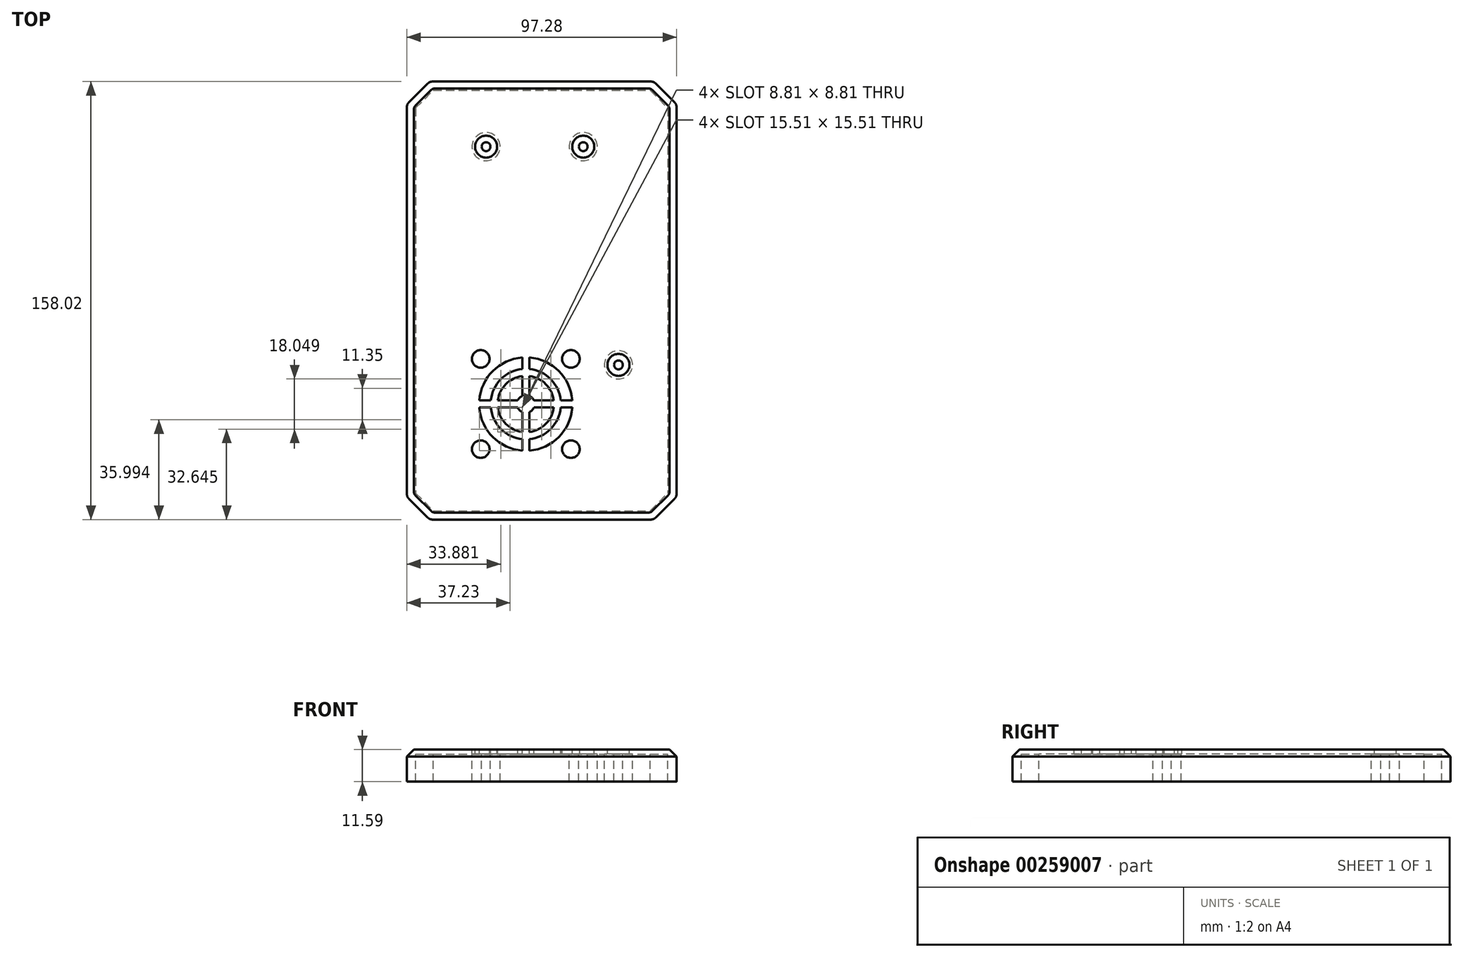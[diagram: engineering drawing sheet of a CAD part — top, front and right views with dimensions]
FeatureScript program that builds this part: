
annotation { "Feature Type Name" : "Feature", "Feature Type Description" : "" }
export const myFeature = defineFeature(function(context is Context, id is Id, definition is map)
    precondition{}
    {
        {
            var Q0;
            Q0=qCreatedBy(makeId("Top.planeOp"),FACE);
            var sketch = newSketch(context, id + "F0", { "sketchPlane" : qUnion([Q0])});
            skLineSegment(sketch, "E0.bottom", {"start": v(-39.11, 75.84) * mm, "end": v(39.11, 75.84) * mm});
            skLineSegment(sketch, "E0.top", {"start": v(-39.11, -75.84) * mm, "end": v(39.11, -75.84) * mm});
            skLineSegment(sketch, "E0.left", {"start": v(-45.46, 69.49) * mm, "end": v(-45.46, -69.49) * mm});
            skLineSegment(sketch, "E0.right", {"start": v(45.46, 69.49) * mm, "end": v(45.46, -69.49) * mm});
            skLineSegment(sketch, "E1", {"start": v(-45.46, 69.49) * mm, "end": v(-39.11, 75.84) * mm});
            skLineSegment(sketch, "E2", {"start": v(39.11, 75.84) * mm, "end": v(45.46, 69.49) * mm});
            skLineSegment(sketch, "E3", {"start": v(-45.46, -69.49) * mm, "end": v(-39.11, -75.84) * mm});
            skLineSegment(sketch, "E4", {"start": v(39.11, -75.84) * mm, "end": v(45.46, -69.49) * mm});
            skPoint(sketch, "E5.orphan", {"position": v(-45.46, 75.84) * mm});
            skPoint(sketch, "E6.orphan", {"position": v(45.46, 75.84) * mm});
            skPoint(sketch, "E7.orphan", {"position": v(45.46, -75.84) * mm});
            skPoint(sketch, "E8.orphan", {"position": v(-45.46, -75.84) * mm});
            skLineSegment(sketch, "E9.0", {"start": v(-48.64, 70.8) * mm, "end": v(-40.43, 79.01) * mm});
            skLineSegment(sketch, "E9.1", {"start": v(-40.43, 79.01) * mm, "end": v(40.43, 79.01) * mm});
            skLineSegment(sketch, "E9.2", {"start": v(-48.64, 70.8) * mm, "end": v(-48.64, -70.8) * mm});
            skLineSegment(sketch, "E9.3", {"start": v(40.43, 79.01) * mm, "end": v(48.64, 70.8) * mm});
            skLineSegment(sketch, "E9.4", {"start": v(-48.64, -70.8) * mm, "end": v(-40.43, -79.01) * mm});
            skLineSegment(sketch, "E9.5", {"start": v(-40.43, -79.01) * mm, "end": v(40.43, -79.01) * mm});
            skLineSegment(sketch, "E9.6", {"start": v(40.43, -79.01) * mm, "end": v(48.64, -70.8) * mm});
            skLineSegment(sketch, "E9.7", {"start": v(48.64, 70.8) * mm, "end": v(48.64, -70.8) * mm});
            skSolve(sketch);
        }
        {
            var Q0;
            Q0=qCreatedBy(makeId("Top.planeOp"),FACE);
            var sketch = newSketch(context, id + "F1", { "sketchPlane" : qUnion([Q0])});
            skCircle(sketch, "E10", {"center": v(-20.06, 55.52) * mm, "radius": 5.08 * mm});
            skCircle(sketch, "E11", {"center": v(14.98, 55.52) * mm, "radius": 5.08 * mm});
            skCircle(sketch, "E12", {"center": v(27.68, -23.22) * mm, "radius": 5.08 * mm});
            skCircle(sketch, "E13", {"center": v(-20.06, 55.52) * mm, "radius": 1.59 * mm});
            skCircle(sketch, "E14", {"center": v(14.98, 55.52) * mm, "radius": 1.59 * mm});
            skCircle(sketch, "E15", {"center": v(27.68, -23.22) * mm, "radius": 1.59 * mm});
            skSolve(sketch);
        }
        {
            var Q0;
            Q0=makeQuery(id+"FWIGaCaiah2UGG0_0.opExtrude","CAP_FACE",FACE,{"disambiguationData":[OSD([sQuery(id+"F0.wireOp",EDGE,"E9.0"),sQuery(id+"F0.wireOp",EDGE,"E9.1"),sQuery(id+"F0.wireOp",EDGE,"E9.2"),sQuery(id+"F0.wireOp",EDGE,"E9.3"),sQuery(id+"F0.wireOp",EDGE,"E9.4"),sQuery(id+"F0.wireOp",EDGE,"E9.5"),sQuery(id+"F0.wireOp",EDGE,"E9.6"),sQuery(id+"F0.wireOp",EDGE,"E9.7")])],"isStart":true});
            var sketch = newSketch(context, id + "F2", { "sketchPlane" : qUnion([Q0])});
            skLineSegment(sketch, "E16.bottom", {"start": v(-39.29, 12.34) * mm, "end": v(10.71, 12.34) * mm});
            skLineSegment(sketch, "E16.top", {"start": v(-39.29, -72.66) * mm, "end": v(10.71, -72.66) * mm});
            skLineSegment(sketch, "E16.left", {"start": v(-42.29, 9.34) * mm, "end": v(-42.29, -69.66) * mm});
            skLineSegment(sketch, "E16.right", {"start": v(13.71, 9.34) * mm, "end": v(13.71, -69.66) * mm});
            skCircle(sketch, "E17", {"center": v(-38.79, -69.16) * mm, "radius": 3.1 * mm});
            skCircle(sketch, "E18", {"center": v(10.21, -69.16) * mm, "radius": 3.1 * mm});
            skCircle(sketch, "E19", {"center": v(10.21, -11.16) * mm, "radius": 3.1 * mm});
            skCircle(sketch, "E20", {"center": v(-38.79, -11.16) * mm, "radius": 3.1 * mm});
            skCircle(sketch, "E21", {"center": v(-38.79, -11.16) * mm, "radius": 1.38 * mm});
            skCircle(sketch, "E22", {"center": v(10.21, -11.16) * mm, "radius": 1.38 * mm});
            skCircle(sketch, "E23", {"center": v(10.21, -69.16) * mm, "radius": 1.38 * mm});
            skCircle(sketch, "E24", {"center": v(-38.79, -69.16) * mm, "radius": 1.38 * mm});
            skPoint(sketch, "E25.visualSharp", {"position": v(-42.29, 12.34) * mm});
            skArc(sketch, "E25.filletArc", {"start": v(-39.29, 12.34) * mm, "mid": v(-41.4, 11.46) * mm, "end": v(-42.29, 9.34) * mm});
            skPoint(sketch, "E26.visualSharp", {"position": v(13.71, 12.34) * mm});
            skArc(sketch, "E26.filletArc", {"start": v(13.71, 9.34) * mm, "mid": v(12.83, 11.46) * mm, "end": v(10.71, 12.34) * mm});
            skPoint(sketch, "E27.visualSharp", {"position": v(-42.29, -72.66) * mm});
            skArc(sketch, "E27.filletArc", {"start": v(-42.29, -69.66) * mm, "mid": v(-41.4, -71.78) * mm, "end": v(-39.29, -72.66) * mm});
            skPoint(sketch, "E28.visualSharp", {"position": v(13.71, -72.66) * mm});
            skArc(sketch, "E28.filletArc", {"start": v(10.71, -72.66) * mm, "mid": v(12.83, -71.78) * mm, "end": v(13.71, -69.66) * mm});
            skSolve(sketch);
        }
        {
            var Q0;
            Q0=makeQuery(id+"F0.imprint","IMPRINT",FACE,{"disambiguationData":[TD([[makeQuery(id+"F0.imprint","IMPRINT",EDGE,{"derivedFrom":sQuery(id+"F0.wireOp",EDGE,"E0.bottom")}),-1.0]])]});
            var Q1;
            Q1=makeQuery(id+"F0.imprint","IMPRINT",FACE,{"disambiguationData":[TD([[makeQuery(id+"F0.imprint","IMPRINT",EDGE,{"derivedFrom":sQuery(id+"F0.wireOp",EDGE,"E0.bottom")}),1.0]])]});
            extrude(context, id + "F3", {"entities" : qUnion([Q0, Q1]), "depth" : 1.59 * mm});
        }
        {
            var Q0;
            Q0=makeQuery(id+"F1.imprint","IMPRINT",FACE,{"disambiguationData":[TD([[makeQuery(id+"F1.imprint","IMPRINT",EDGE,{"derivedFrom":sQuery(id+"F1.wireOp",EDGE,"E12")}),1.0]])]});
            var Q1;
            Q1=makeQuery(id+"F1.imprint","IMPRINT",FACE,{"disambiguationData":[TD([[makeQuery(id+"F1.imprint","IMPRINT",EDGE,{"derivedFrom":sQuery(id+"F1.wireOp",EDGE,"E11")}),1.0]])]});
            var Q2;
            Q2=makeQuery(id+"F1.imprint","IMPRINT",FACE,{"disambiguationData":[TD([[makeQuery(id+"F1.imprint","IMPRINT",EDGE,{"derivedFrom":sQuery(id+"F1.wireOp",EDGE,"E10")}),1.0]])]});
            extrude(context, id + "F4", {"entities" : qUnion([Q0, Q1, Q2]), "operationType" : NewBodyOperationType.ADD, "oppositeDirection" : true, "depth" : 10 * mm});
        }
        {
            var Q0;
            Q0 = qSketchRegion(id + "F2", true);
            var Q1;
            Q1 = qSketchRegion(id + "F0", true);
            extrude(context, id + "F5", {"entities" : qUnion([Q0, Q1]), "operationType" : NewBodyOperationType.ADD, "oppositeDirection" : true, "depth" : 10 * mm});
        }
        {
            var Q0;
            Q0=makeQuery(id+"F3.opExtrude","CAP_FACE",FACE,{"disambiguationData":[OSD([sQuery(id+"F0.wireOp",EDGE,"E9.0"),sQuery(id+"F0.wireOp",EDGE,"E9.1"),sQuery(id+"F0.wireOp",EDGE,"E9.2"),sQuery(id+"F0.wireOp",EDGE,"E9.3"),sQuery(id+"F0.wireOp",EDGE,"E9.4"),sQuery(id+"F0.wireOp",EDGE,"E9.5"),sQuery(id+"F0.wireOp",EDGE,"E9.6"),sQuery(id+"F0.wireOp",EDGE,"E9.7")])],"isStart":false});
            var sketch = newSketch(context, id + "F6", { "sketchPlane" : qUnion([Q0])});
            skCircle(sketch, "E29", {"center": v(-20.06, 55.52) * mm, "radius": 3.97 * mm});
            skCircle(sketch, "E30", {"center": v(14.98, 55.52) * mm, "radius": 3.97 * mm});
            skCircle(sketch, "E31", {"center": v(27.68, -23.22) * mm, "radius": 3.97 * mm});
            skSolve(sketch);
        }
        {
            var Q0;
            Q0 = qSketchRegion(id + "F6", true);
            extrude(context, id + "F7", {"entities" : qUnion([Q0]), "operationType" : NewBodyOperationType.REMOVE, "oppositeDirection" : true, "depth" : 1.59 * mm});
        }
        {
            var Q0;
            Q0=makeQuery(id+"F3.opExtrude","CAP_FACE",FACE,{"disambiguationData":[OSD([sQuery(id+"F0.wireOp",EDGE,"E9.0"),sQuery(id+"F0.wireOp",EDGE,"E9.1"),sQuery(id+"F0.wireOp",EDGE,"E9.2"),sQuery(id+"F0.wireOp",EDGE,"E9.3"),sQuery(id+"F0.wireOp",EDGE,"E9.4"),sQuery(id+"F0.wireOp",EDGE,"E9.5"),sQuery(id+"F0.wireOp",EDGE,"E9.6"),sQuery(id+"F0.wireOp",EDGE,"E9.7")])],"isStart":false});
            var sketch = newSketch(context, id + "F8", { "sketchPlane" : qUnion([Q0])});
            skCircle(sketch, "E32", {"center": v(-22, -21.07) * mm, "radius": 3.18 * mm});
            skCircle(sketch, "E33", {"center": v(10.54, -21.07) * mm, "radius": 3.18 * mm});
            skCircle(sketch, "E34", {"center": v(10.54, -53.61) * mm, "radius": 3.18 * mm});
            skCircle(sketch, "E35", {"center": v(-22, -53.61) * mm, "radius": 3.18 * mm});
            skArc(sketch, "E36", {"start": v(-22.51, -38.61) * mm, "mid": v(-17.63, -49.24) * mm, "end": v(-7, -54.12) * mm});
            skArc(sketch, "E37", {"start": v(-7, -34.43) * mm, "mid": v(-7.98, -35.1) * mm, "end": v(-8.64, -36.07) * mm});
            skLineSegment(sketch, "E38", {"start": v(-7, -34.43) * mm, "end": v(-7, -27.26) * mm});
            skLineSegment(sketch, "E39", {"start": v(-4.46, -34.43) * mm, "end": v(-4.46, -27.26) * mm});
            skLineSegment(sketch, "E40", {"start": v(-2.82, -36.07) * mm, "end": v(4.35, -36.07) * mm});
            skLineSegment(sketch, "E41", {"start": v(-2.82, -38.61) * mm, "end": v(4.35, -38.61) * mm});
            skLineSegment(sketch, "E42", {"start": v(-7, -40.25) * mm, "end": v(-7, -47.42) * mm});
            skLineSegment(sketch, "E43", {"start": v(-4.46, -40.25) * mm, "end": v(-4.46, -47.42) * mm});
            skLineSegment(sketch, "E44", {"start": v(-8.64, -36.07) * mm, "end": v(-15.81, -36.07) * mm});
            skLineSegment(sketch, "E45", {"start": v(-8.64, -38.61) * mm, "end": v(-15.81, -38.61) * mm});
            skArc(sketch, "E46", {"start": v(-15.81, -38.61) * mm, "mid": v(-12.92, -44.52) * mm, "end": v(-7, -47.42) * mm});
            skArc(sketch, "E47", {"start": v(-18.37, -38.61) * mm, "mid": v(-14.71, -46.32) * mm, "end": v(-7, -49.98) * mm});
            skLineSegment(sketch, "E48.trimOffspring", {"start": v(-18.37, -36.07) * mm, "end": v(-22.51, -36.07) * mm});
            skLineSegment(sketch, "E49.trimOffspring", {"start": v(-18.37, -38.61) * mm, "end": v(-22.51, -38.61) * mm});
            skArc(sketch, "E50.trimOffspring", {"start": v(4.35, -36.07) * mm, "mid": v(1.45, -30.16) * mm, "end": v(-4.46, -27.26) * mm});
            skArc(sketch, "E51.trimOffspring", {"start": v(6.9, -36.07) * mm, "mid": v(3.25, -28.36) * mm, "end": v(-4.46, -24.7) * mm});
            skLineSegment(sketch, "E52.trimOffspring", {"start": v(6.9, -36.07) * mm, "end": v(11.05, -36.07) * mm});
            skLineSegment(sketch, "E53.trimOffspring", {"start": v(6.9, -38.61) * mm, "end": v(11.05, -38.61) * mm});
            skLineSegment(sketch, "E54.trimOffspring", {"start": v(-4.46, -24.7) * mm, "end": v(-4.46, -20.56) * mm});
            skLineSegment(sketch, "E55.trimOffspring", {"start": v(-7, -24.7) * mm, "end": v(-7, -20.56) * mm});
            skArc(sketch, "E56.trimOffspring", {"start": v(-7, -24.7) * mm, "mid": v(-14.71, -28.36) * mm, "end": v(-18.37, -36.07) * mm});
            skArc(sketch, "E57.trimOffspring", {"start": v(-7, -27.26) * mm, "mid": v(-12.92, -30.16) * mm, "end": v(-15.81, -36.07) * mm});
            skArc(sketch, "E58.trimOffspring", {"start": v(-8.64, -38.61) * mm, "mid": v(-7.98, -39.59) * mm, "end": v(-7, -40.25) * mm});
            skArc(sketch, "E59.trimOffspring", {"start": v(-2.82, -36.07) * mm, "mid": v(-3.49, -35.1) * mm, "end": v(-4.46, -34.43) * mm});
            skArc(sketch, "E60.trimOffspring", {"start": v(-4.46, -40.25) * mm, "mid": v(-3.49, -39.59) * mm, "end": v(-2.82, -38.61) * mm});
            skLineSegment(sketch, "E61.trimOffspring", {"start": v(-7, -49.98) * mm, "end": v(-7, -54.12) * mm});
            skLineSegment(sketch, "E62.trimOffspring", {"start": v(-4.46, -49.98) * mm, "end": v(-4.46, -54.12) * mm});
            skArc(sketch, "E63.trimOffspring", {"start": v(-7, -20.56) * mm, "mid": v(-17.63, -25.44) * mm, "end": v(-22.51, -36.07) * mm});
            skArc(sketch, "E64.trimOffspring", {"start": v(11.05, -36.07) * mm, "mid": v(6.16, -25.44) * mm, "end": v(-4.46, -20.56) * mm});
            skArc(sketch, "E65.trimOffspring", {"start": v(-4.46, -54.12) * mm, "mid": v(6.16, -49.24) * mm, "end": v(11.05, -38.61) * mm});
            skArc(sketch, "E66.trimOffspring", {"start": v(-4.46, -49.98) * mm, "mid": v(3.25, -46.32) * mm, "end": v(6.9, -38.61) * mm});
            skArc(sketch, "E67.trimOffspring", {"start": v(-4.46, -47.42) * mm, "mid": v(1.45, -44.52) * mm, "end": v(4.35, -38.61) * mm});
            skSolve(sketch);
        }
        {
            var Q0;
            Q0 = qSketchRegion(id + "F8", true);
            extrude(context, id + "F9", {"entities" : qUnion([Q0]), "operationType" : NewBodyOperationType.REMOVE, "endBound" : BoundingType.THROUGH_ALL, "oppositeDirection" : true, "depth" : 25.4 * mm});
        }
        {
            var Q0;
            Q0=makeQuery(id+"F3.opExtrude","CAP_EDGE",EDGE,{"disambiguationData":[OSD([sQuery(id+"F0.wireOp",EDGE,"E9.1")])],"isStart":false});
            var Q1;
            Q1=makeQuery(id+"F3.opExtrude","CAP_EDGE",EDGE,{"disambiguationData":[OSD([sQuery(id+"F0.wireOp",EDGE,"E9.0")])],"isStart":false});
            var Q2;
            Q2=makeQuery(id+"F3.opExtrude","CAP_EDGE",EDGE,{"disambiguationData":[OSD([sQuery(id+"F0.wireOp",EDGE,"E9.2")])],"isStart":false});
            var Q3;
            Q3=makeQuery(id+"F3.opExtrude","CAP_EDGE",EDGE,{"disambiguationData":[OSD([sQuery(id+"F0.wireOp",EDGE,"E9.3")])],"isStart":false});
            var Q4;
            Q4=makeQuery(id+"F3.opExtrude","CAP_EDGE",EDGE,{"disambiguationData":[OSD([sQuery(id+"F0.wireOp",EDGE,"E9.7")])],"isStart":false});
            var Q5;
            Q5=makeQuery(id+"F3.opExtrude","CAP_EDGE",EDGE,{"disambiguationData":[OSD([sQuery(id+"F0.wireOp",EDGE,"E9.4")])],"isStart":false});
            var Q6;
            Q6=makeQuery(id+"F3.opExtrude","CAP_EDGE",EDGE,{"disambiguationData":[OSD([sQuery(id+"F0.wireOp",EDGE,"E9.5")])],"isStart":false});
            var Q7;
            Q7=makeQuery(id+"F3.opExtrude","CAP_EDGE",EDGE,{"disambiguationData":[OSD([sQuery(id+"F0.wireOp",EDGE,"E9.6")])],"isStart":false});
            chamfer(context, id + "F10", {"entities" : qUnion([Q0, Q1, Q2, Q3, Q4, Q5, Q6, Q7]), "width" : 2.54 * mm, "tangentPropagation" : true});
        }
        {
            var Q0;
            {var subQ0=sQuery(id+"F0.wireOp",EDGE,"E9.7");var subQ1=sQuery(id+"F0.wireOp",EDGE,"E9.3");Q0=makeQuery(id+"F5.boolean.opBoolean","MERGE",EDGE,{"derivedFrom":[makeQuery(id+"F3.opExtrude","SWEPT_EDGE",EDGE,{"disambiguationData":[OSD([subQ1,subQ0])]}),makeQuery(id+"F5.opExtrude","SWEPT_EDGE",EDGE,{"disambiguationData":[OSD([subQ1,subQ0])]})]});}
            var Q1;
            Q1=makeQuery(id+"F10.opChamfer","BLEND_EDGE",EDGE,{"blendedFrom":[makeQuery(id+"F3.opExtrude","CAP_EDGE",EDGE,{"disambiguationData":[OSD([sQuery(id+"F0.wireOp",EDGE,"E9.3")])],"isStart":false}),makeQuery(id+"F3.opExtrude","CAP_EDGE",EDGE,{"disambiguationData":[OSD([sQuery(id+"F0.wireOp",EDGE,"E9.7")])],"isStart":false})],"blendedInto":[]});
            var Q2;
            {var subQ0=sQuery(id+"F0.wireOp",EDGE,"E9.3");var subQ1=sQuery(id+"F0.wireOp",EDGE,"E9.1");Q2=makeQuery(id+"F5.boolean.opBoolean","MERGE",EDGE,{"derivedFrom":[makeQuery(id+"F3.opExtrude","SWEPT_EDGE",EDGE,{"disambiguationData":[OSD([subQ1,subQ0])]}),makeQuery(id+"F5.opExtrude","SWEPT_EDGE",EDGE,{"disambiguationData":[OSD([subQ1,subQ0])]})]});}
            var Q3;
            Q3=makeQuery(id+"F10.opChamfer","BLEND_EDGE",EDGE,{"blendedFrom":[makeQuery(id+"F3.opExtrude","CAP_EDGE",EDGE,{"disambiguationData":[OSD([sQuery(id+"F0.wireOp",EDGE,"E9.1")])],"isStart":false}),makeQuery(id+"F3.opExtrude","CAP_EDGE",EDGE,{"disambiguationData":[OSD([sQuery(id+"F0.wireOp",EDGE,"E9.3")])],"isStart":false})],"blendedInto":[]});
            var Q4;
            {var subQ0=sQuery(id+"F0.wireOp",EDGE,"E9.1");var subQ1=sQuery(id+"F0.wireOp",EDGE,"E9.0");Q4=makeQuery(id+"F5.boolean.opBoolean","MERGE",EDGE,{"derivedFrom":[makeQuery(id+"F3.opExtrude","SWEPT_EDGE",EDGE,{"disambiguationData":[OSD([subQ1,subQ0])]}),makeQuery(id+"F5.opExtrude","SWEPT_EDGE",EDGE,{"disambiguationData":[OSD([subQ1,subQ0])]})]});}
            var Q5;
            Q5=makeQuery(id+"F10.opChamfer","BLEND_EDGE",EDGE,{"blendedFrom":[makeQuery(id+"F3.opExtrude","CAP_EDGE",EDGE,{"disambiguationData":[OSD([sQuery(id+"F0.wireOp",EDGE,"E9.0")])],"isStart":false}),makeQuery(id+"F3.opExtrude","CAP_EDGE",EDGE,{"disambiguationData":[OSD([sQuery(id+"F0.wireOp",EDGE,"E9.1")])],"isStart":false})],"blendedInto":[]});
            var Q6;
            Q6=makeQuery(id+"F10.opChamfer","BLEND_EDGE",EDGE,{"blendedFrom":[makeQuery(id+"F3.opExtrude","CAP_EDGE",EDGE,{"disambiguationData":[OSD([sQuery(id+"F0.wireOp",EDGE,"E9.0")])],"isStart":false}),makeQuery(id+"F3.opExtrude","CAP_EDGE",EDGE,{"disambiguationData":[OSD([sQuery(id+"F0.wireOp",EDGE,"E9.2")])],"isStart":false})],"blendedInto":[]});
            var Q7;
            {var subQ0=sQuery(id+"F0.wireOp",EDGE,"E9.2");var subQ1=sQuery(id+"F0.wireOp",EDGE,"E9.0");Q7=makeQuery(id+"F5.boolean.opBoolean","MERGE",EDGE,{"derivedFrom":[makeQuery(id+"F3.opExtrude","SWEPT_EDGE",EDGE,{"disambiguationData":[OSD([subQ1,subQ0])]}),makeQuery(id+"F5.opExtrude","SWEPT_EDGE",EDGE,{"disambiguationData":[OSD([subQ1,subQ0])]})]});}
            var Q8;
            {var subQ0=sQuery(id+"F0.wireOp",EDGE,"E9.4");var subQ1=sQuery(id+"F0.wireOp",EDGE,"E9.2");Q8=makeQuery(id+"F5.boolean.opBoolean","MERGE",EDGE,{"derivedFrom":[makeQuery(id+"F3.opExtrude","SWEPT_EDGE",EDGE,{"disambiguationData":[OSD([subQ1,subQ0])]}),makeQuery(id+"F5.opExtrude","SWEPT_EDGE",EDGE,{"disambiguationData":[OSD([subQ1,subQ0])]})]});}
            var Q9;
            Q9=makeQuery(id+"F10.opChamfer","BLEND_EDGE",EDGE,{"blendedFrom":[makeQuery(id+"F3.opExtrude","CAP_EDGE",EDGE,{"disambiguationData":[OSD([sQuery(id+"F0.wireOp",EDGE,"E9.2")])],"isStart":false}),makeQuery(id+"F3.opExtrude","CAP_EDGE",EDGE,{"disambiguationData":[OSD([sQuery(id+"F0.wireOp",EDGE,"E9.4")])],"isStart":false})],"blendedInto":[]});
            var Q10;
            Q10=makeQuery(id+"F10.opChamfer","BLEND_EDGE",EDGE,{"blendedFrom":[makeQuery(id+"F3.opExtrude","CAP_EDGE",EDGE,{"disambiguationData":[OSD([sQuery(id+"F0.wireOp",EDGE,"E9.4")])],"isStart":false}),makeQuery(id+"F3.opExtrude","CAP_EDGE",EDGE,{"disambiguationData":[OSD([sQuery(id+"F0.wireOp",EDGE,"E9.5")])],"isStart":false})],"blendedInto":[]});
            var Q11;
            {var subQ0=sQuery(id+"F0.wireOp",EDGE,"E9.5");var subQ1=sQuery(id+"F0.wireOp",EDGE,"E9.4");Q11=makeQuery(id+"F5.boolean.opBoolean","MERGE",EDGE,{"derivedFrom":[makeQuery(id+"F3.opExtrude","SWEPT_EDGE",EDGE,{"disambiguationData":[OSD([subQ1,subQ0])]}),makeQuery(id+"F5.opExtrude","SWEPT_EDGE",EDGE,{"disambiguationData":[OSD([subQ1,subQ0])]})]});}
            var Q12;
            {var subQ0=sQuery(id+"F0.wireOp",EDGE,"E9.6");var subQ1=sQuery(id+"F0.wireOp",EDGE,"E9.5");Q12=makeQuery(id+"F5.boolean.opBoolean","MERGE",EDGE,{"derivedFrom":[makeQuery(id+"F3.opExtrude","SWEPT_EDGE",EDGE,{"disambiguationData":[OSD([subQ1,subQ0])]}),makeQuery(id+"F5.opExtrude","SWEPT_EDGE",EDGE,{"disambiguationData":[OSD([subQ1,subQ0])]})]});}
            var Q13;
            Q13=makeQuery(id+"F10.opChamfer","BLEND_EDGE",EDGE,{"blendedFrom":[makeQuery(id+"F3.opExtrude","CAP_EDGE",EDGE,{"disambiguationData":[OSD([sQuery(id+"F0.wireOp",EDGE,"E9.5")])],"isStart":false}),makeQuery(id+"F3.opExtrude","CAP_EDGE",EDGE,{"disambiguationData":[OSD([sQuery(id+"F0.wireOp",EDGE,"E9.6")])],"isStart":false})],"blendedInto":[]});
            var Q14;
            Q14=makeQuery(id+"F10.opChamfer","BLEND_EDGE",EDGE,{"blendedFrom":[makeQuery(id+"F3.opExtrude","CAP_EDGE",EDGE,{"disambiguationData":[OSD([sQuery(id+"F0.wireOp",EDGE,"E9.6")])],"isStart":false}),makeQuery(id+"F3.opExtrude","CAP_EDGE",EDGE,{"disambiguationData":[OSD([sQuery(id+"F0.wireOp",EDGE,"E9.7")])],"isStart":false})],"blendedInto":[]});
            var Q15;
            {var subQ0=sQuery(id+"F0.wireOp",EDGE,"E9.7");var subQ1=sQuery(id+"F0.wireOp",EDGE,"E9.6");Q15=makeQuery(id+"F5.boolean.opBoolean","MERGE",EDGE,{"derivedFrom":[makeQuery(id+"F3.opExtrude","SWEPT_EDGE",EDGE,{"disambiguationData":[OSD([subQ1,subQ0])]}),makeQuery(id+"F5.opExtrude","SWEPT_EDGE",EDGE,{"disambiguationData":[OSD([subQ1,subQ0])]})]});}
            fillet(context, id + "F11", {"entities" : qUnion([Q0, Q1, Q2, Q3, Q4, Q5, Q6, Q7, Q8, Q9, Q10, Q11, Q12, Q13, Q14, Q15]), "radius" : 2.54 * mm, "tangentPropagation" : true, "allowEdgeOverflow" : false});
        }
    });
